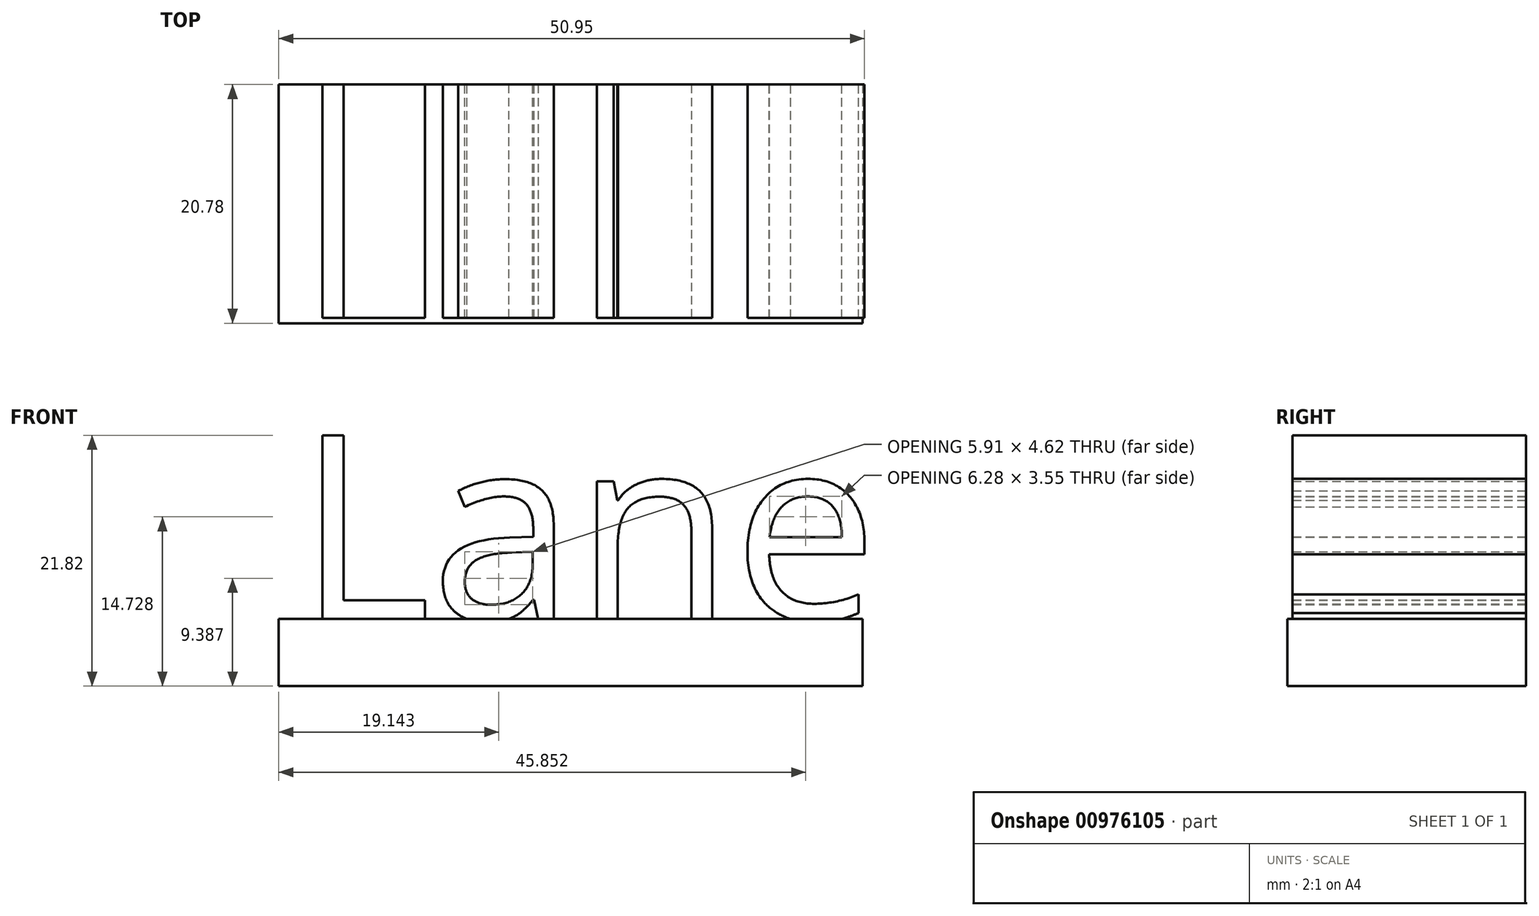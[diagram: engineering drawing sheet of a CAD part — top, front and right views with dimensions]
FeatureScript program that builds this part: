
annotation { "Feature Type Name" : "Feature", "Feature Type Description" : "" }
export const myFeature = defineFeature(function(context is Context, id is Id, definition is map)
    precondition{}
    {
        {
            var Q0;
            Q0=qCreatedBy(makeId("Top.planeOp"),FACE);
            var sketch = newSketch(context, id + "F0", { "sketchPlane" : qUnion([Q0])});
            skLineSegment(sketch, "E0.bottom", {"start": v(-26.99, 0) * mm, "end": v(23.81, 0) * mm});
            skLineSegment(sketch, "E0.top", {"start": v(-26.99, -20.78) * mm, "end": v(23.81, -20.78) * mm});
            skLineSegment(sketch, "E0.left", {"start": v(-26.99, 0) * mm, "end": v(-26.99, -20.78) * mm});
            skLineSegment(sketch, "E0.right", {"start": v(23.81, 0) * mm, "end": v(23.81, -20.78) * mm});
            skSolve(sketch);
        }
        {
            var Q0;
            Q0 = qSketchRegion(id + "F0", true);
            extrude(context, id + "F1", {"entities" : qUnion([Q0]), "depth" : 5.84 * mm, "offsetDistance" : 25.4 * mm});
        }
        {
            var Q0;
            Q0=qCreatedBy(makeId("Front.planeOp"),FACE);
            var sketch = newSketch(context, id + "F2", { "sketchPlane" : qUnion([Q0])});
            skText(sketch, "E1", { "text": "Lane", "fontName": "OpenSans-Regular.ttf"});
            const initialGuessF2  = {"E1": [-0.0254, 0.00579, 1, 0, 0.01617]};
            skSetInitialGuess(sketch, initialGuessF2);
            skSolve(sketch);
        }
        {
            var Q0;
            Q0 = qSketchRegion(id + "F2", true);
            extrude(context, id + "F3", {"entities" : qUnion([Q0]), "operationType" : NewBodyOperationType.ADD, "depth" : 20.32 * mm, "offsetDistance" : 25.4 * mm});
        }
    });
